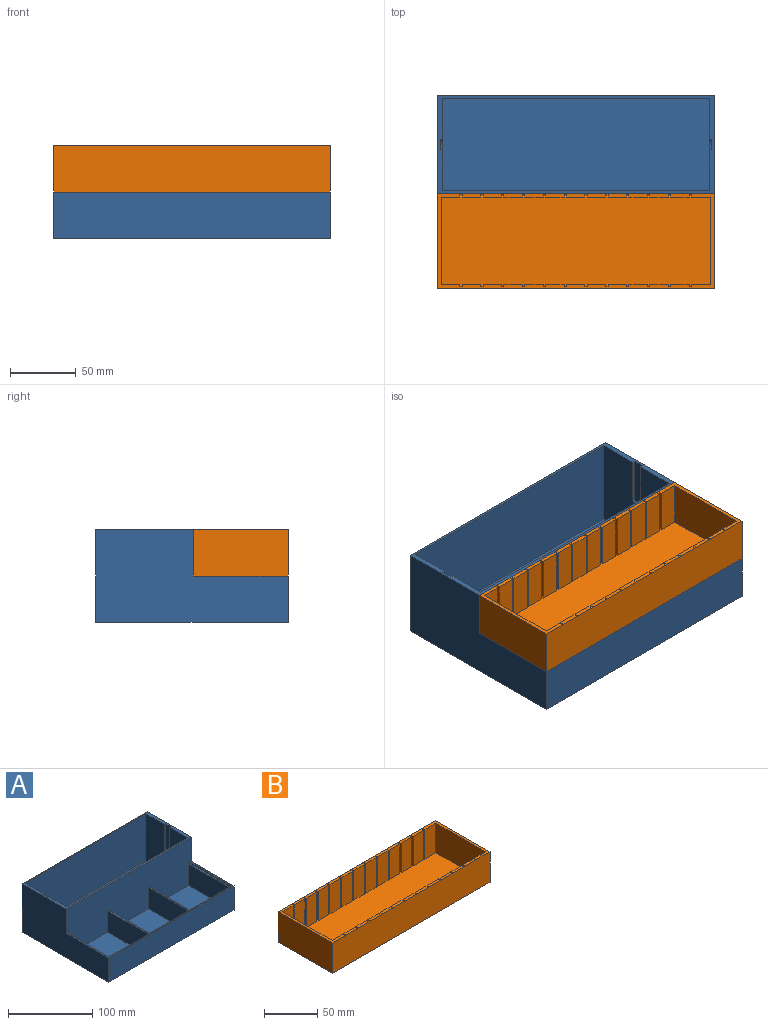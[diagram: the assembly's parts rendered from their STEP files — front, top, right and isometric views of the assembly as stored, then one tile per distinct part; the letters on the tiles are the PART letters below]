
ASSEMBLY  parts=2 mates=1
PART A: 37 faces, bbox 210x146x70 mm
  f0: plane 68x31mm, normal (1,0,0), area 2108mm2, adj f1,f14,f18,f36
  f1: plane 66x31mm, normal (0,1,0), area 2046mm2, adj f0,f2,f18,f36
  f2: plane 68x31mm, normal (-1,0,0), area 2108mm2, adj f1,f14,f18,f36
  f3: plane 68x31mm, normal (1,0,0), area 2108mm2, adj f4,f14,f19,f36
  f4: plane 66x31mm, normal (0,1,0), area 2046mm2, adj f3,f5,f19,f36
  f5: plane 68x31mm, normal (-1,0,0), area 2108mm2, adj f4,f14,f19,f36
  f6: plane 68x31mm, normal (1,0,0), area 2108mm2, adj f7,f14,f20,f36
  f7: plane 66x31mm, normal (0,1,0), area 2046mm2, adj f6,f8,f20,f36
  f8: plane 68x31mm, normal (-1,0,0), area 2108mm2, adj f7,f14,f20,f36
  f9: plane 210x146mm, normal (0,0,-1), area 30660mm2, adj f15,f28,f31,f32
  f10: plane 202x68mm, normal (0,-1,0), area 13736mm2, adj f11,f13,f16,f17
  f11: plane 70x68mm, normal (1,0,0), area 4462.9mm2, adj f10,f12,f16,f17,f22,f23,f24
  f12: plane 202x68mm, normal (0,1,0), area 13736mm2, adj f11,f13,f16,f17
  f13: plane 70x68mm, normal (-1,0,0), area 4462.9mm2, adj f10,f12,f16,f17,f25,f26,f27
  f14: plane 210x68mm, normal (0,-1,0), area 13900mm2, adj f0,f2,f3,f5,f6,f8,f16,f18
  f15: plane 210x70mm, normal (0,1,0), area 14700mm2, adj f9,f16,f28,f31
  f16: plane 210x74mm, normal (0,0,1), area 1368mm2, adj f10,f11,f12,f13,f14,f15,f22,f23
  f17: plane 202x70mm, normal (0,0,1), area 14140mm2, adj f10,f11,f12,f13
  f18: plane 68x66mm, normal (0,0,1), area 4488mm2, adj f0,f1,f2,f14
  f19: plane 68x66mm, normal (0,0,1), area 4488mm2, adj f3,f4,f5,f14
  f20: plane 68x66mm, normal (0,0,1), area 4488mm2, adj f6,f7,f8,f14
  f21: plane 210x72mm, normal (0,0,1), area 700mm2, adj f14,f28,f31,f32,f33,f34,f35
  f22: plane 34x2mm, normal (0,-1,0), area 68mm2, adj f11,f16,f24,f30
  f23: plane 34x2mm, normal (0,1,0), area 68mm2, adj f11,f16,f24,f30
  f24: cylinder r=4mm len=8mm, axis (1,0,0), area 25.1mm2, adj f11,f22,f23,f30
  f25: cylinder r=4mm len=8mm, axis (1,0,0), area 25.1mm2, adj f13,f26,f27,f29
  f26: plane 34x2mm, normal (0,-1,0), area 68mm2, adj f13,f16,f25,f29
  f27: plane 34x2mm, normal (0,1,0), area 68mm2, adj f13,f16,f25,f29
  f28: plane 146x70mm, normal (1,0,0), area 7700mm2, adj f9,f14,f15,f16,f21,f32
  f29: plane 38x8mm, normal (-1,0,0), area 297.1mm2, adj f16,f25,f26,f27
  f30: plane 38x8mm, normal (1,0,0), area 297.1mm2, adj f16,f22,f23,f24
  f31: plane 146x70mm, normal (-1,0,0), area 7700mm2, adj f9,f14,f15,f16,f21,f32
  f32: plane 210x35mm, normal (0,-1,0), area 7350mm2, adj f9,f21,f28,f31
  f33: plane 70x2mm, normal (1,0,0), area 140mm2, adj f14,f21,f34,f36
  f34: plane 206x2mm, normal (0,1,0), area 412mm2, adj f21,f33,f35,f36
  f35: plane 70x2mm, normal (-1,0,0), area 140mm2, adj f14,f21,f34,f36
  f36: plane 206x70mm, normal (0,0,1), area 956mm2, adj f0,f1,f2,f3,f4,f5,f6,f7
PART B: 112 faces, bbox 210x72x37 mm
  f0: plane 34x14.5mm, normal (0,-1,0), area 493mm2, adj f24,f27,f39,f102
  f1: plane 34x14.1mm, normal (0,-1,0), area 479.4mm2, adj f24,f27,f99,f101
  f2: plane 34x14.1mm, normal (0,-1,0), area 479.4mm2, adj f24,f27,f96,f98
  f3: plane 34x14.1mm, normal (0,-1,0), area 479.4mm2, adj f24,f27,f93,f95
  f4: plane 34x14.1mm, normal (0,-1,0), area 479.4mm2, adj f24,f27,f90,f92
  f5: plane 34x14.1mm, normal (0,-1,0), area 479.4mm2, adj f24,f27,f63,f89
  f6: plane 34x14.1mm, normal (0,-1,0), area 479.4mm2, adj f24,f27,f60,f62
  f7: plane 34x14.1mm, normal (0,-1,0), area 479.4mm2, adj f24,f27,f57,f59
  f8: plane 34x14.1mm, normal (0,-1,0), area 479.4mm2, adj f24,f27,f54,f56
  f9: plane 34x14.1mm, normal (0,-1,0), area 479.4mm2, adj f24,f27,f51,f53
  f10: plane 34x14.1mm, normal (0,-1,0), area 479.4mm2, adj f24,f27,f48,f50
  f11: plane 34x14.1mm, normal (0,-1,0), area 479.4mm2, adj f24,f27,f45,f47
  f12: plane 34x14.1mm, normal (0,1,0), area 479.4mm2, adj f24,f27,f106,f111
  f13: plane 34x14.1mm, normal (0,1,0), area 479.4mm2, adj f24,f27,f103,f108
  f14: plane 34x14.5mm, normal (0,1,0), area 493mm2, adj f24,f27,f39,f105
  f15: plane 34x14.1mm, normal (0,1,0), area 479.4mm2, adj f24,f27,f87,f109
  f16: plane 34x14.1mm, normal (0,1,0), area 479.4mm2, adj f24,f27,f84,f85
  f17: plane 34x14.1mm, normal (0,1,0), area 479.4mm2, adj f24,f27,f76,f81
  f18: plane 34x14.1mm, normal (0,1,0), area 479.4mm2, adj f24,f27,f78,f82
  f19: plane 34x14.1mm, normal (0,1,0), area 479.4mm2, adj f24,f27,f75,f79
  f20: plane 34x14.1mm, normal (0,1,0), area 479.4mm2, adj f24,f27,f72,f73
  f21: plane 34x14.1mm, normal (0,1,0), area 479.4mm2, adj f24,f27,f69,f70
  f22: plane 34x14.1mm, normal (0,1,0), area 479.4mm2, adj f24,f27,f66,f67
  f23: plane 34x14.1mm, normal (0,1,0), area 479.4mm2, adj f24,f27,f40,f64
  f24: plane 210x72mm, normal (0,0,1), area 1574.4mm2, adj f0,f1,f2,f3,f4,f5,f6,f7
  f25: plane 34x14mm, normal (0,-1,0), area 476mm2, adj f24,f27,f28,f44
  f26: plane 34x14mm, normal (0,1,0), area 476mm2, adj f24,f27,f28,f41
  f27: plane 204x70mm, normal (0,0,1), area 13545.6mm2, adj f0,f1,f2,f3,f4,f5,f6,f7
  f28: plane 66x34mm, normal (1,0,0), area 2244mm2, adj f24,f25,f26,f27
  f29: plane 206x2mm, normal (0,1,0), area 412mm2, adj f30,f32,f33,f38
  f30: plane 68x2mm, normal (-1,0,0), area 136mm2, adj f29,f31,f33,f38
  f31: plane 206x2mm, normal (0,-1,0), area 412mm2, adj f30,f32,f33,f38
  f32: plane 68x2mm, normal (1,0,0), area 136mm2, adj f29,f31,f33,f38
  f33: plane 206x68mm, normal (0,0,-1), area 14008mm2, adj f29,f30,f31,f32
  f34: plane 72x35mm, normal (1,0,0), area 2520mm2, adj f24,f35,f37,f38
  f35: plane 210x35mm, normal (0,1,0), area 7350mm2, adj f24,f34,f36,f38
  f36: plane 72x35mm, normal (-1,0,0), area 2520mm2, adj f24,f35,f37,f38
  f37: plane 210x35mm, normal (0,-1,0), area 7350mm2, adj f24,f34,f36,f38
  f38: plane 210x72mm, normal (0,0,-1), area 1112mm2, adj f29,f30,f31,f32,f34,f35,f36,f37
  f39: plane 66x34mm, normal (-1,0,0), area 2244mm2, adj f0,f14,f24,f27
  f40: plane 34x2mm, normal (-1,0,0), area 68mm2, adj f23,f24,f27,f42
  f41: plane 34x2mm, normal (1,0,0), area 68mm2, adj f24,f26,f27,f42
  f42: plane 34x1.7mm, normal (0,1,0), area 57.8mm2, adj f24,f27,f40,f41
  f43: plane 34x1.7mm, normal (0,-1,0), area 57.8mm2, adj f24,f27,f44,f45
  f44: plane 34x2mm, normal (1,0,0), area 68mm2, adj f24,f25,f27,f43
  f45: plane 34x2mm, normal (-1,0,0), area 68mm2, adj f11,f24,f27,f43
  f46: plane 34x1.7mm, normal (0,-1,0), area 57.8mm2, adj f24,f27,f47,f48
  f47: plane 34x2mm, normal (1,0,0), area 68mm2, adj f11,f24,f27,f46
  f48: plane 34x2mm, normal (-1,0,0), area 68mm2, adj f10,f24,f27,f46
  f49: plane 34x1.7mm, normal (0,-1,0), area 57.8mm2, adj f24,f27,f50,f51
  f50: plane 34x2mm, normal (1,0,0), area 68mm2, adj f10,f24,f27,f49
  f51: plane 34x2mm, normal (-1,0,0), area 68mm2, adj f9,f24,f27,f49
  f52: plane 34x1.7mm, normal (0,-1,0), area 57.8mm2, adj f24,f27,f53,f54
  f53: plane 34x2mm, normal (1,0,0), area 68mm2, adj f9,f24,f27,f52
  f54: plane 34x2mm, normal (-1,0,0), area 68mm2, adj f8,f24,f27,f52
  f55: plane 34x1.7mm, normal (0,-1,0), area 57.8mm2, adj f24,f27,f56,f57
  f56: plane 34x2mm, normal (1,0,0), area 68mm2, adj f8,f24,f27,f55
  f57: plane 34x2mm, normal (-1,0,0), area 68mm2, adj f7,f24,f27,f55
  f58: plane 34x1.7mm, normal (0,-1,0), area 57.8mm2, adj f24,f27,f59,f60
  f59: plane 34x2mm, normal (1,0,0), area 68mm2, adj f7,f24,f27,f58
  f60: plane 34x2mm, normal (-1,0,0), area 68mm2, adj f6,f24,f27,f58
  f61: plane 34x1.7mm, normal (0,-1,0), area 57.8mm2, adj f24,f27,f62,f63
  f62: plane 34x2mm, normal (1,0,0), area 68mm2, adj f6,f24,f27,f61
  f63: plane 34x2mm, normal (-1,0,0), area 68mm2, adj f5,f24,f27,f61
  f64: plane 34x2mm, normal (1,0,0), area 68mm2, adj f23,f24,f27,f65
  f65: plane 34x1.7mm, normal (0,1,0), area 57.8mm2, adj f24,f27,f64,f66
  f66: plane 34x2mm, normal (-1,0,0), area 68mm2, adj f22,f24,f27,f65
  f67: plane 34x2mm, normal (1,0,0), area 68mm2, adj f22,f24,f27,f68
  f68: plane 34x1.7mm, normal (0,1,0), area 57.8mm2, adj f24,f27,f67,f69
  f69: plane 34x2mm, normal (-1,0,0), area 68mm2, adj f21,f24,f27,f68
  f70: plane 34x2mm, normal (1,0,0), area 68mm2, adj f21,f24,f27,f71
  f71: plane 34x1.7mm, normal (0,1,0), area 57.8mm2, adj f24,f27,f70,f72
  f72: plane 34x2mm, normal (-1,0,0), area 68mm2, adj f20,f24,f27,f71
  f73: plane 34x2mm, normal (1,0,0), area 68mm2, adj f20,f24,f27,f74
  f74: plane 34x1.7mm, normal (0,1,0), area 57.8mm2, adj f24,f27,f73,f75
  f75: plane 34x2mm, normal (-1,0,0), area 68mm2, adj f19,f24,f27,f74
  f76: plane 34x2mm, normal (1,0,0), area 68mm2, adj f17,f24,f27,f77
  f77: plane 34x1.7mm, normal (0,1,0), area 57.8mm2, adj f24,f27,f76,f78
  f78: plane 34x2mm, normal (-1,0,0), area 68mm2, adj f18,f24,f27,f77
  f79: plane 34x2mm, normal (1,0,0), area 68mm2, adj f19,f24,f27,f80
  f80: plane 34x1.7mm, normal (0,1,0), area 57.8mm2, adj f24,f27,f79,f81
  f81: plane 34x2mm, normal (-1,0,0), area 68mm2, adj f17,f24,f27,f80
  f82: plane 34x2mm, normal (1,0,0), area 68mm2, adj f18,f24,f27,f83
  f83: plane 34x1.7mm, normal (0,1,0), area 57.8mm2, adj f24,f27,f82,f84
  f84: plane 34x2mm, normal (-1,0,0), area 68mm2, adj f16,f24,f27,f83
  f85: plane 34x2mm, normal (1,0,0), area 68mm2, adj f16,f24,f27,f86
  f86: plane 34x1.7mm, normal (0,1,0), area 57.8mm2, adj f24,f27,f85,f87
  f87: plane 34x2mm, normal (-1,0,0), area 68mm2, adj f15,f24,f27,f86
  f88: plane 34x1.7mm, normal (0,-1,0), area 57.8mm2, adj f24,f27,f89,f90
  f89: plane 34x2mm, normal (1,0,0), area 68mm2, adj f5,f24,f27,f88
  f90: plane 34x2mm, normal (-1,0,0), area 68mm2, adj f4,f24,f27,f88
  f91: plane 34x1.7mm, normal (0,-1,0), area 57.8mm2, adj f24,f27,f92,f93
  f92: plane 34x2mm, normal (1,0,0), area 68mm2, adj f4,f24,f27,f91
  f93: plane 34x2mm, normal (-1,0,0), area 68mm2, adj f3,f24,f27,f91
  f94: plane 34x1.7mm, normal (0,-1,0), area 57.8mm2, adj f24,f27,f95,f96
  f95: plane 34x2mm, normal (1,0,0), area 68mm2, adj f3,f24,f27,f94
  f96: plane 34x2mm, normal (-1,0,0), area 68mm2, adj f2,f24,f27,f94
  f97: plane 34x1.7mm, normal (0,-1,0), area 57.8mm2, adj f24,f27,f98,f99
  f98: plane 34x2mm, normal (1,0,0), area 68mm2, adj f2,f24,f27,f97
  f99: plane 34x2mm, normal (-1,0,0), area 68mm2, adj f1,f24,f27,f97
  f100: plane 34x1.7mm, normal (0,-1,0), area 57.8mm2, adj f24,f27,f101,f102
  f101: plane 34x2mm, normal (1,0,0), area 68mm2, adj f1,f24,f27,f100
  f102: plane 34x2mm, normal (-1,0,0), area 68mm2, adj f0,f24,f27,f100
  f103: plane 34x2mm, normal (1,0,0), area 68mm2, adj f13,f24,f27,f104
  f104: plane 34x1.7mm, normal (0,1,0), area 57.8mm2, adj f24,f27,f103,f105
  f105: plane 34x2mm, normal (-1,0,0), area 68mm2, adj f14,f24,f27,f104
  f106: plane 34x2mm, normal (1,0,0), area 68mm2, adj f12,f24,f27,f107
  f107: plane 34x1.7mm, normal (0,1,0), area 57.8mm2, adj f24,f27,f106,f108
  f108: plane 34x2mm, normal (-1,0,0), area 68mm2, adj f13,f24,f27,f107
  f109: plane 34x2mm, normal (1,0,0), area 68mm2, adj f15,f24,f27,f110
  f110: plane 34x1.7mm, normal (0,1,0), area 57.8mm2, adj f24,f27,f109,f111
  f111: plane 34x2mm, normal (-1,0,0), area 68mm2, adj f12,f24,f27,f110
PLACE A t=(0,1,0)mm
PLACE B t=(0,-36,33)mm
MATE slider B.f33 <-> A.f36  axis (0,0,-1) through (-103,-71,33)mm
